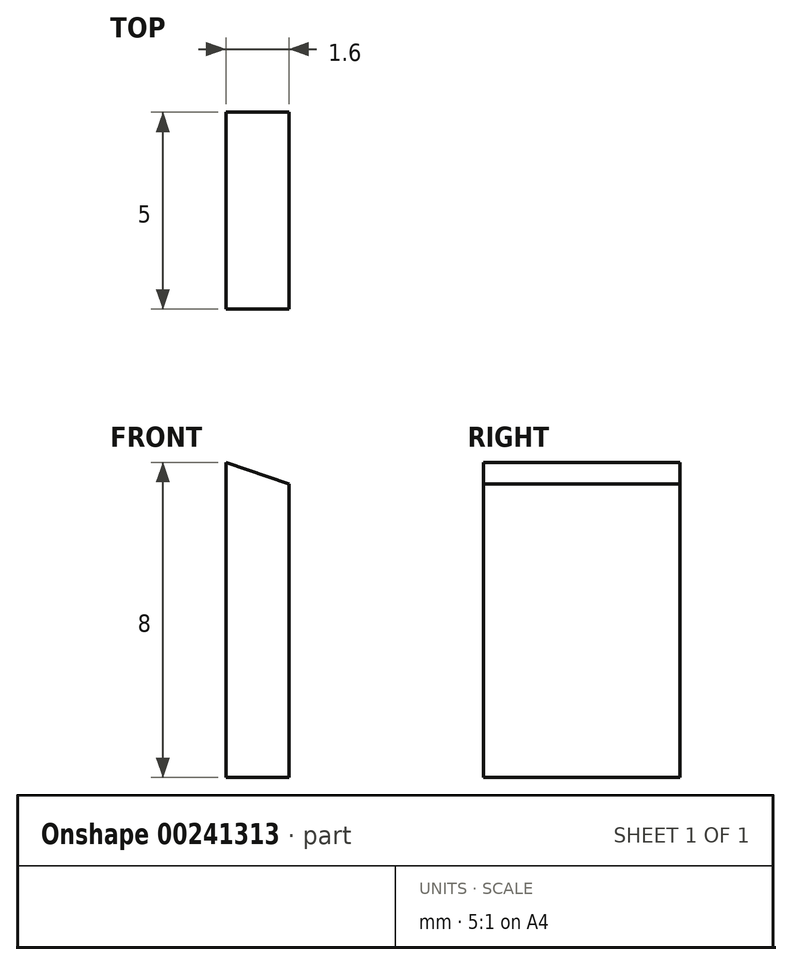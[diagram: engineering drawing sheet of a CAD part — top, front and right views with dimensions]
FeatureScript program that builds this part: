
annotation { "Feature Type Name" : "Feature", "Feature Type Description" : "" }
export const myFeature = defineFeature(function(context is Context, id is Id, definition is map)
    precondition{}
    {
        {
            var Q0;
            Q0=qCreatedBy(makeId("Front.planeOp"),FACE);
            var sketch = newSketch(context, id + "F0", { "sketchPlane" : qUnion([Q0])});
            skLineSegment(sketch, "E0.bottom", {"start": v(0, 0) * mm, "end": v(1.6, 0) * mm});
            skLineSegment(sketch, "E0.left", {"start": v(0, 0) * mm, "end": v(0, 8) * mm});
            skLineSegment(sketch, "E0.right", {"start": v(1.6, 0) * mm, "end": v(1.6, 7.45) * mm});
            skLineSegment(sketch, "E1", {"start": v(0, 8) * mm, "end": v(1.6, 7.45) * mm});
            skSolve(sketch);
        }
        {
            var Q0;
            Q0=makeQuery(id+"F0.imprint","IMPRINT",FACE,{"disambiguationData":[TD([[makeQuery(id+"F0.imprint","IMPRINT",EDGE,{"derivedFrom":sQuery(id+"F0.wireOp",EDGE,"E0.bottom")}),1.0]])]});
            extrude(context, id + "F1", {"entities" : qUnion([Q0]), "depth" : 5 * mm});
        }
    });
